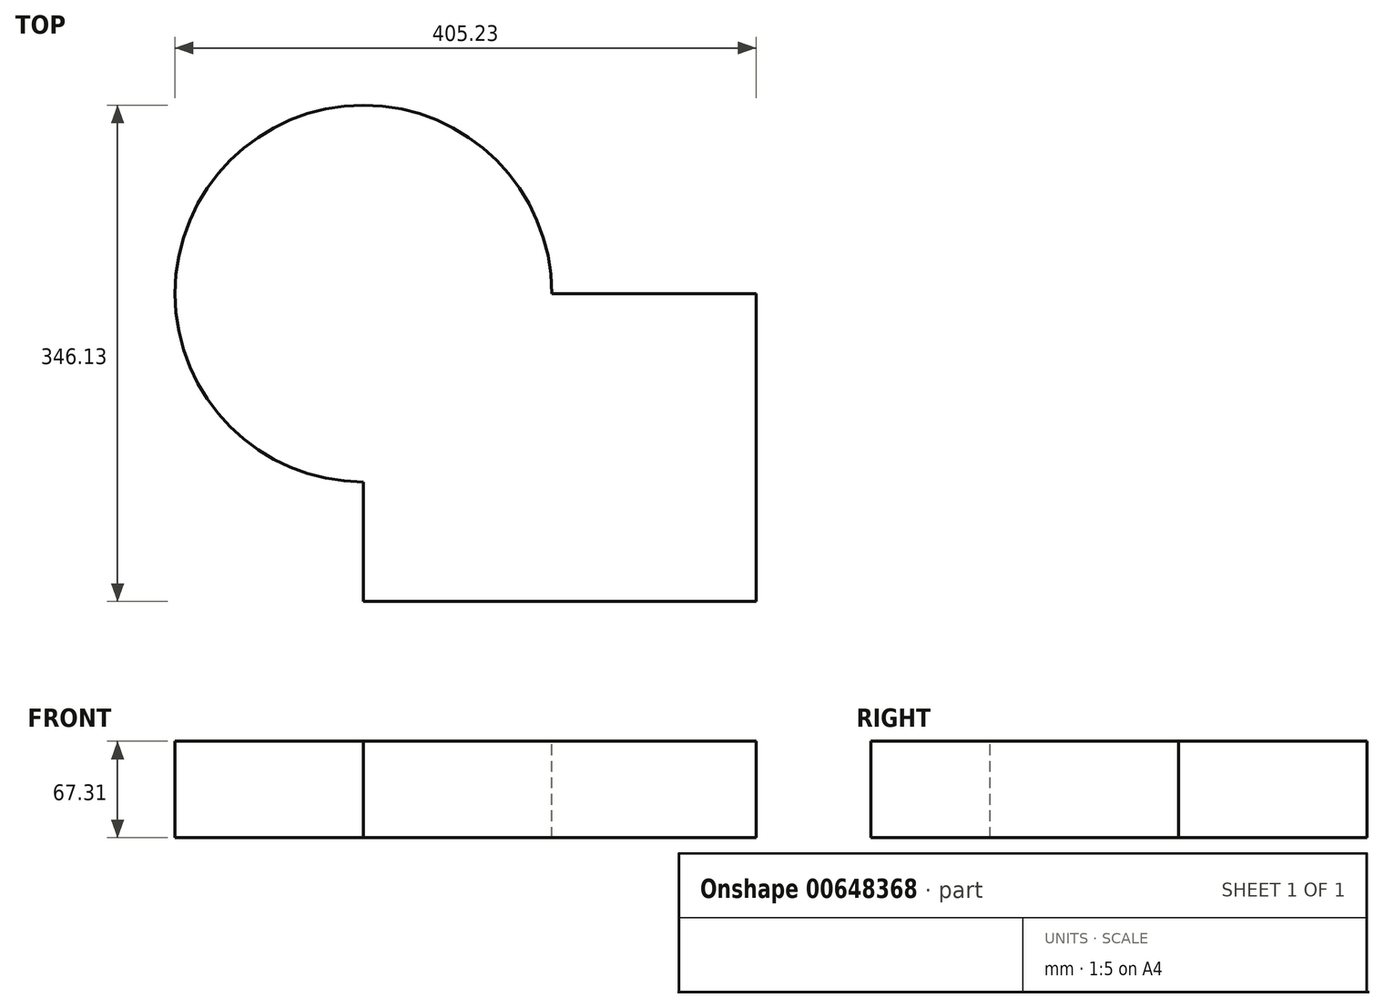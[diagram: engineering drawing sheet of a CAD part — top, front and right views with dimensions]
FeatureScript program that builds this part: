
annotation { "Feature Type Name" : "Feature", "Feature Type Description" : "" }
export const myFeature = defineFeature(function(context is Context, id is Id, definition is map)
    precondition{}
    {
        {
            var Q0;
            Q0=qCreatedBy(makeId("Top.planeOp"),FACE);
            var sketch = newSketch(context, id + "F0", { "sketchPlane" : qUnion([Q0])});
            skLineSegment(sketch, "E0.bottom", {"start": v(117.77, -104.93) * mm, "end": v(-156.06, -104.93) * mm});
            skLineSegment(sketch, "E0.top", {"start": v(117.77, 109.8) * mm, "end": v(-156.06, 109.8) * mm});
            skLineSegment(sketch, "E0.left", {"start": v(117.77, -104.93) * mm, "end": v(117.77, 109.8) * mm});
            skLineSegment(sketch, "E0.right", {"start": v(-156.06, -104.93) * mm, "end": v(-156.06, 109.8) * mm});
            skCircle(sketch, "E1", {"center": v(-156.06, 109.8) * mm, "radius": 131.4 * mm});
            skSolve(sketch);
        }
        {
            var Q0;
            Q0 = qSketchRegion(id + "F0", true);
            extrude(context, id + "F1", {"entities" : qUnion([Q0]), "oppositeDirection" : true, "depth" : 67.3 * mm, "offsetDistance" : 25.4 * mm});
        }
    });
